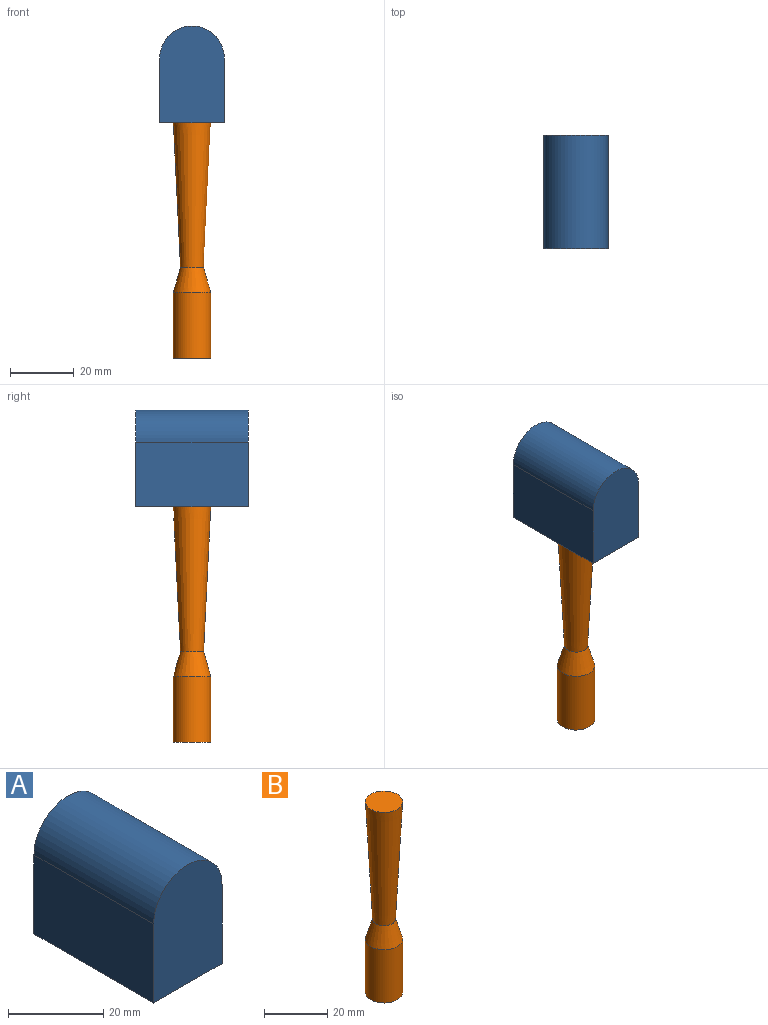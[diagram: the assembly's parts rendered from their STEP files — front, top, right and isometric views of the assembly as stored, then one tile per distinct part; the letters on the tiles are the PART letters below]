
ASSEMBLY  parts=2 mates=1
PART A: 6 faces, bbox 20.3x35.6x30.5 mm
  f0: plane 35.56x20.32mm, normal (1,0,0), area 722.6mm2, adj f1,f3,f4,f5
  f1: cylinder r=10.16mm len=35.56mm, axis (0,1,0), area 1135mm2, adj f0,f2,f4,f5
  f2: plane 35.56x20.32mm, normal (-1,0,0), area 722.6mm2, adj f1,f3,f4,f5
  f3: plane 35.56x20.32mm, normal (0,0,-1), area 722.6mm2, adj f0,f2,f4,f5
  f4: plane 30.48x20.32mm, normal (0,-1,0), area 575mm2, adj f0,f1,f2,f3
  f5: plane 30.48x20.32mm, normal (0,1,0), area 575mm2, adj f0,f1,f2,f3
PART B: 5 faces, bbox 11.8x11.8x74 mm
  f0: plane 11.8x11.8mm, normal (0,0,1), area 109.3mm2, adj f1
  f1: cone r=3.64mm half-angle=2.8deg, axis (0,0,1), area 1367.1mm2, adj f0,f2
  f2: cone r=5.9mm half-angle=16.3deg, axis (0,0,-1), area 242.1mm2, adj f1,f3
  f3: cylinder r=5.9mm len=20.69mm, axis (0,0,1), area 766.9mm2, adj f2,f4
  f4: plane 11.8x11.8mm, normal (0,0,-1), area 109.3mm2, adj f3
PLACE A at identity
PLACE B t=(0,27.56,-39.76)mm
MATE fastened B.f3 <-> A.f3  axis (0,0,1) through (0,-17.78,0)mm
